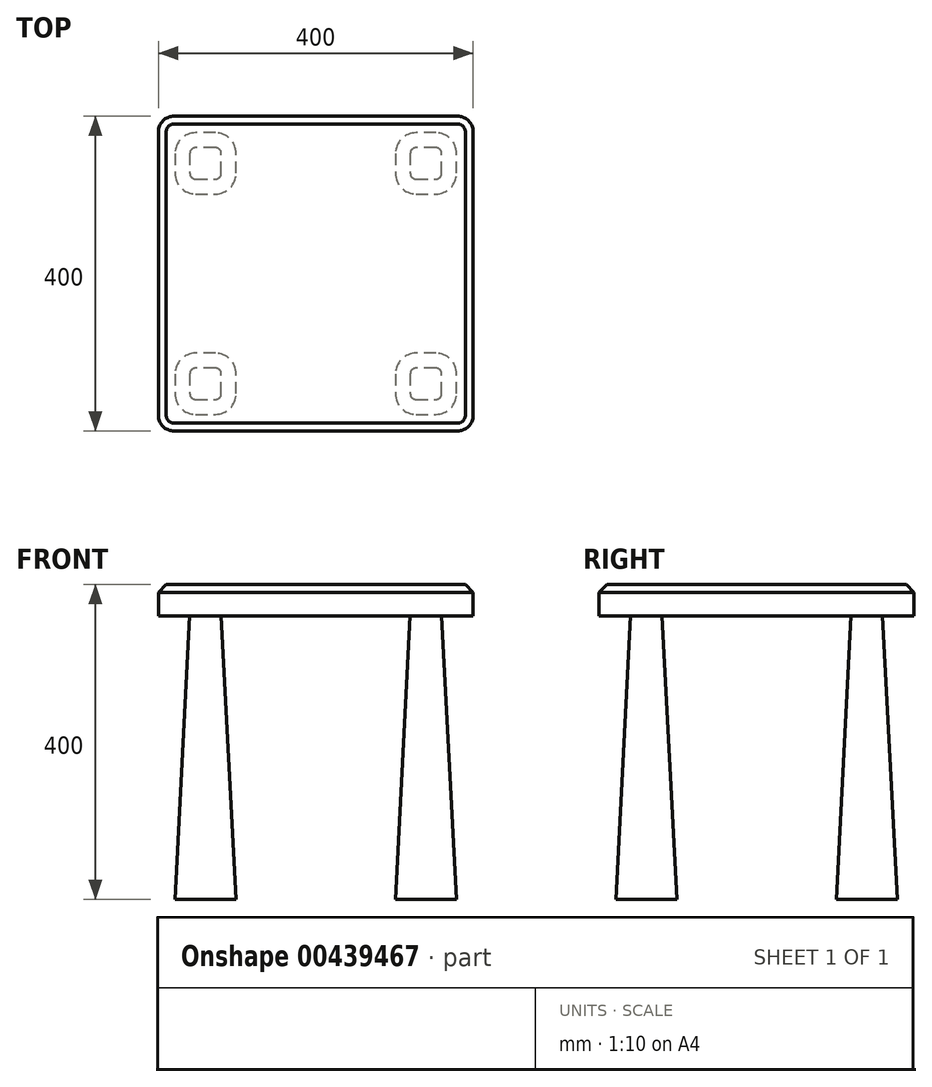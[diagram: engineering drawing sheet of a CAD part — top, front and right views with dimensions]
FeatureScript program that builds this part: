
annotation { "Feature Type Name" : "Feature", "Feature Type Description" : "" }
export const myFeature = defineFeature(function(context is Context, id is Id, definition is map)
    precondition{}
    {
        {
            var Q0;
            Q0=qCreatedBy(makeId("Top.planeOp"),FACE);
            var sketch = newSketch(context, id + "F0", { "sketchPlane" : qUnion([Q0])});
            skLineSegment(sketch, "E0.bottom", {"start": v(-11.7, 356.3) * mm, "end": v(348.3, 356.3) * mm});
            skLineSegment(sketch, "E0.top", {"start": v(-11.7, -43.7) * mm, "end": v(348.3, -43.7) * mm});
            skLineSegment(sketch, "E0.left", {"start": v(-31.7, 336.3) * mm, "end": v(-31.7, -23.7) * mm});
            skLineSegment(sketch, "E0.right", {"start": v(368.3, 336.3) * mm, "end": v(368.3, -23.7) * mm});
            skPoint(sketch, "E1.visualSharp", {"position": v(-31.7, 356.3) * mm});
            skArc(sketch, "E1.filletArc", {"start": v(-11.7, 356.3) * mm, "mid": v(-25.84, 350.44) * mm, "end": v(-31.7, 336.3) * mm});
            skPoint(sketch, "E2.visualSharp", {"position": v(368.3, 356.3) * mm});
            skArc(sketch, "E2.filletArc", {"start": v(368.3, 336.3) * mm, "mid": v(362.44, 350.44) * mm, "end": v(348.3, 356.3) * mm});
            skPoint(sketch, "E3.visualSharp", {"position": v(368.3, -43.7) * mm});
            skArc(sketch, "E3.filletArc", {"start": v(348.3, -43.7) * mm, "mid": v(362.44, -37.85) * mm, "end": v(368.3, -23.7) * mm});
            skPoint(sketch, "E4.visualSharp", {"position": v(-31.7, -43.7) * mm});
            skArc(sketch, "E4.filletArc", {"start": v(-31.7, -23.7) * mm, "mid": v(-25.84, -37.85) * mm, "end": v(-11.7, -43.7) * mm});
            skSolve(sketch);
        }
        {
            var Q0;
            Q0=makeQuery(id+"F0.imprint","IMPRINT",FACE,{"disambiguationData":[TD([[makeQuery(id+"F0.imprint","IMPRINT",EDGE,{"derivedFrom":sQuery(id+"F0.wireOp",EDGE,"E0.bottom")}),-1.0]])]});
            extrude(context, id + "F1", {"entities" : qUnion([Q0]), "depth" : 40 * mm});
        }
        {
            var Q0;
            Q0=makeQuery(id+"F1.opExtrude","CAP_FACE",FACE,{"disambiguationData":[OSD([sQuery(id+"F0.wireOp",EDGE,"E0.bottom"),sQuery(id+"F0.wireOp",EDGE,"E0.top"),sQuery(id+"F0.wireOp",EDGE,"E0.left"),sQuery(id+"F0.wireOp",EDGE,"E0.right"),sQuery(id+"F0.wireOp",EDGE,"E1.filletArc"),sQuery(id+"F0.wireOp",EDGE,"E2.filletArc"),sQuery(id+"F0.wireOp",EDGE,"E3.filletArc"),sQuery(id+"F0.wireOp",EDGE,"E4.filletArc")])],"isStart":true});
            var sketch = newSketch(context, id + "F2", { "sketchPlane" : qUnion([Q0])});
            skLineSegment(sketch, "E5.bottom", {"start": v(15.8, 3.7) * mm, "end": v(40.8, 3.7) * mm});
            skLineSegment(sketch, "E5.top", {"start": v(15.8, -36.3) * mm, "end": v(40.8, -36.3) * mm});
            skLineSegment(sketch, "E5.left", {"start": v(8.3, -3.8) * mm, "end": v(8.3, -28.8) * mm});
            skLineSegment(sketch, "E5.right", {"start": v(48.3, -3.8) * mm, "end": v(48.3, -28.8) * mm});
            skPoint(sketch, "E6.visualSharp", {"position": v(8.3, 3.7) * mm});
            skArc(sketch, "E6.filletArc", {"start": v(15.8, 3.7) * mm, "mid": v(10.5, 1.5) * mm, "end": v(8.3, -3.8) * mm});
            skPoint(sketch, "E7.visualSharp", {"position": v(48.3, 3.7) * mm});
            skArc(sketch, "E7.filletArc", {"start": v(48.3, -3.8) * mm, "mid": v(46.1, 1.5) * mm, "end": v(40.8, 3.7) * mm});
            skPoint(sketch, "E8.visualSharp", {"position": v(48.3, -36.3) * mm});
            skArc(sketch, "E8.filletArc", {"start": v(40.8, -36.3) * mm, "mid": v(46.1, -34.1) * mm, "end": v(48.3, -28.8) * mm});
            skPoint(sketch, "E9.visualSharp", {"position": v(8.3, -36.3) * mm});
            skArc(sketch, "E9.filletArc", {"start": v(8.3, -28.8) * mm, "mid": v(10.5, -34.1) * mm, "end": v(15.8, -36.3) * mm});
            skPoint(sketch, "E10.0.1.0", {"position": v(8.3, -316.3) * mm});
            skPoint(sketch, "E10.0.1.1", {"position": v(48.3, -316.3) * mm});
            skPoint(sketch, "E10.0.1.2", {"position": v(48.3, -276.3) * mm});
            skPoint(sketch, "E10.0.1.3", {"position": v(8.3, -276.3) * mm});
            skLineSegment(sketch, "E10.0.1.4", {"start": v(15.8, -316.3) * mm, "end": v(40.8, -316.3) * mm});
            skLineSegment(sketch, "E10.0.1.5", {"start": v(8.3, -283.8) * mm, "end": v(8.3, -308.8) * mm});
            skLineSegment(sketch, "E10.0.1.6", {"start": v(48.3, -283.8) * mm, "end": v(48.3, -308.8) * mm});
            skLineSegment(sketch, "E10.0.1.7", {"start": v(15.8, -276.3) * mm, "end": v(40.8, -276.3) * mm});
            skArc(sketch, "E10.0.1.8", {"start": v(48.3, -283.8) * mm, "mid": v(46.1, -278.5) * mm, "end": v(40.8, -276.3) * mm});
            skArc(sketch, "E10.0.1.9", {"start": v(40.8, -316.3) * mm, "mid": v(46.1, -314.1) * mm, "end": v(48.3, -308.8) * mm});
            skArc(sketch, "E10.0.1.10", {"start": v(8.3, -308.8) * mm, "mid": v(10.5, -314.1) * mm, "end": v(15.8, -316.3) * mm});
            skArc(sketch, "E10.0.1.11", {"start": v(15.8, -276.3) * mm, "mid": v(10.5, -278.5) * mm, "end": v(8.3, -283.8) * mm});
            skPoint(sketch, "E10.1.0.0", {"position": v(288.3, -36.3) * mm});
            skPoint(sketch, "E10.1.0.1", {"position": v(328.3, -36.3) * mm});
            skPoint(sketch, "E10.1.0.2", {"position": v(328.3, 3.7) * mm});
            skPoint(sketch, "E10.1.0.3", {"position": v(288.3, 3.7) * mm});
            skLineSegment(sketch, "E10.1.0.4", {"start": v(295.8, -36.3) * mm, "end": v(320.8, -36.3) * mm});
            skLineSegment(sketch, "E10.1.0.5", {"start": v(288.3, -3.8) * mm, "end": v(288.3, -28.8) * mm});
            skLineSegment(sketch, "E10.1.0.6", {"start": v(328.3, -3.8) * mm, "end": v(328.3, -28.8) * mm});
            skLineSegment(sketch, "E10.1.0.7", {"start": v(295.8, 3.7) * mm, "end": v(320.8, 3.7) * mm});
            skArc(sketch, "E10.1.0.8", {"start": v(328.3, -3.8) * mm, "mid": v(326.1, 1.5) * mm, "end": v(320.8, 3.7) * mm});
            skArc(sketch, "E10.1.0.9", {"start": v(320.8, -36.3) * mm, "mid": v(326.1, -34.1) * mm, "end": v(328.3, -28.8) * mm});
            skArc(sketch, "E10.1.0.10", {"start": v(288.3, -28.8) * mm, "mid": v(290.5, -34.1) * mm, "end": v(295.8, -36.3) * mm});
            skArc(sketch, "E10.1.0.11", {"start": v(295.8, 3.7) * mm, "mid": v(290.5, 1.5) * mm, "end": v(288.3, -3.8) * mm});
            skPoint(sketch, "E10.1.1.0", {"position": v(288.3, -316.3) * mm});
            skPoint(sketch, "E10.1.1.1", {"position": v(328.3, -316.3) * mm});
            skPoint(sketch, "E10.1.1.2", {"position": v(328.3, -276.3) * mm});
            skPoint(sketch, "E10.1.1.3", {"position": v(288.3, -276.3) * mm});
            skLineSegment(sketch, "E10.1.1.4", {"start": v(295.8, -316.3) * mm, "end": v(320.8, -316.3) * mm});
            skLineSegment(sketch, "E10.1.1.5", {"start": v(288.3, -283.8) * mm, "end": v(288.3, -308.8) * mm});
            skLineSegment(sketch, "E10.1.1.6", {"start": v(328.3, -283.8) * mm, "end": v(328.3, -308.8) * mm});
            skLineSegment(sketch, "E10.1.1.7", {"start": v(295.8, -276.3) * mm, "end": v(320.8, -276.3) * mm});
            skArc(sketch, "E10.1.1.8", {"start": v(328.3, -283.8) * mm, "mid": v(326.1, -278.5) * mm, "end": v(320.8, -276.3) * mm});
            skArc(sketch, "E10.1.1.9", {"start": v(320.8, -316.3) * mm, "mid": v(326.1, -314.1) * mm, "end": v(328.3, -308.8) * mm});
            skArc(sketch, "E10.1.1.10", {"start": v(288.3, -308.8) * mm, "mid": v(290.5, -314.1) * mm, "end": v(295.8, -316.3) * mm});
            skArc(sketch, "E10.1.1.11", {"start": v(295.8, -276.3) * mm, "mid": v(290.5, -278.5) * mm, "end": v(288.3, -283.8) * mm});
            skLineSegment(sketch, "E10.direction1", {"start": v(8.3, -36.3) * mm, "end": v(288.3, -36.3) * mm, "construction": true});
            skLineSegment(sketch, "E10.direction2", {"start": v(8.3, -36.3) * mm, "end": v(8.3, -316.3) * mm, "construction": true});
            skSolve(sketch);
        }
        {
            var Q0;
            Q0=makeQuery(id+"F2.imprint","IMPRINT",FACE,{"disambiguationData":[TD([[makeQuery(id+"F2.imprint","IMPRINT",EDGE,{"derivedFrom":sQuery(id+"F2.wireOp",EDGE,"E5.bottom")}),-1.0]])]});
            var Q1;
            Q1=makeQuery(id+"F2.imprint","IMPRINT",FACE,{"disambiguationData":[TD([[makeQuery(id+"F2.imprint","IMPRINT",EDGE,{"derivedFrom":sQuery(id+"F2.wireOp",EDGE,"E10.1.0.4")}),1.0]])]});
            var Q2;
            Q2=makeQuery(id+"F2.imprint","IMPRINT",FACE,{"disambiguationData":[TD([[makeQuery(id+"F2.imprint","IMPRINT",EDGE,{"derivedFrom":sQuery(id+"F2.wireOp",EDGE,"E10.1.1.4")}),1.0]])]});
            var Q3;
            Q3=makeQuery(id+"F2.imprint","IMPRINT",FACE,{"disambiguationData":[TD([[makeQuery(id+"F2.imprint","IMPRINT",EDGE,{"derivedFrom":sQuery(id+"F2.wireOp",EDGE,"E10.0.1.4")}),1.0]])]});
            extrude(context, id + "F3", {"entities" : qUnion([Q0, Q1, Q2, Q3]), "operationType" : NewBodyOperationType.ADD, "depth" : 360 * mm, "hasDraft" : true, "draftAngle" : 3 * degree});
        }
        {
            var Q0;
            Q0=makeQuery(id+"F1.opExtrude","CAP_FACE",FACE,{"disambiguationData":[OSD([sQuery(id+"F0.wireOp",EDGE,"E0.bottom"),sQuery(id+"F0.wireOp",EDGE,"E0.top"),sQuery(id+"F0.wireOp",EDGE,"E0.left"),sQuery(id+"F0.wireOp",EDGE,"E0.right"),sQuery(id+"F0.wireOp",EDGE,"E1.filletArc"),sQuery(id+"F0.wireOp",EDGE,"E2.filletArc"),sQuery(id+"F0.wireOp",EDGE,"E3.filletArc"),sQuery(id+"F0.wireOp",EDGE,"E4.filletArc")])],"isStart":false});
            chamfer(context, id + "F4", {"entities" : qUnion([Q0]), "width" : 10 * mm, "tangentPropagation" : true});
        }
    });
